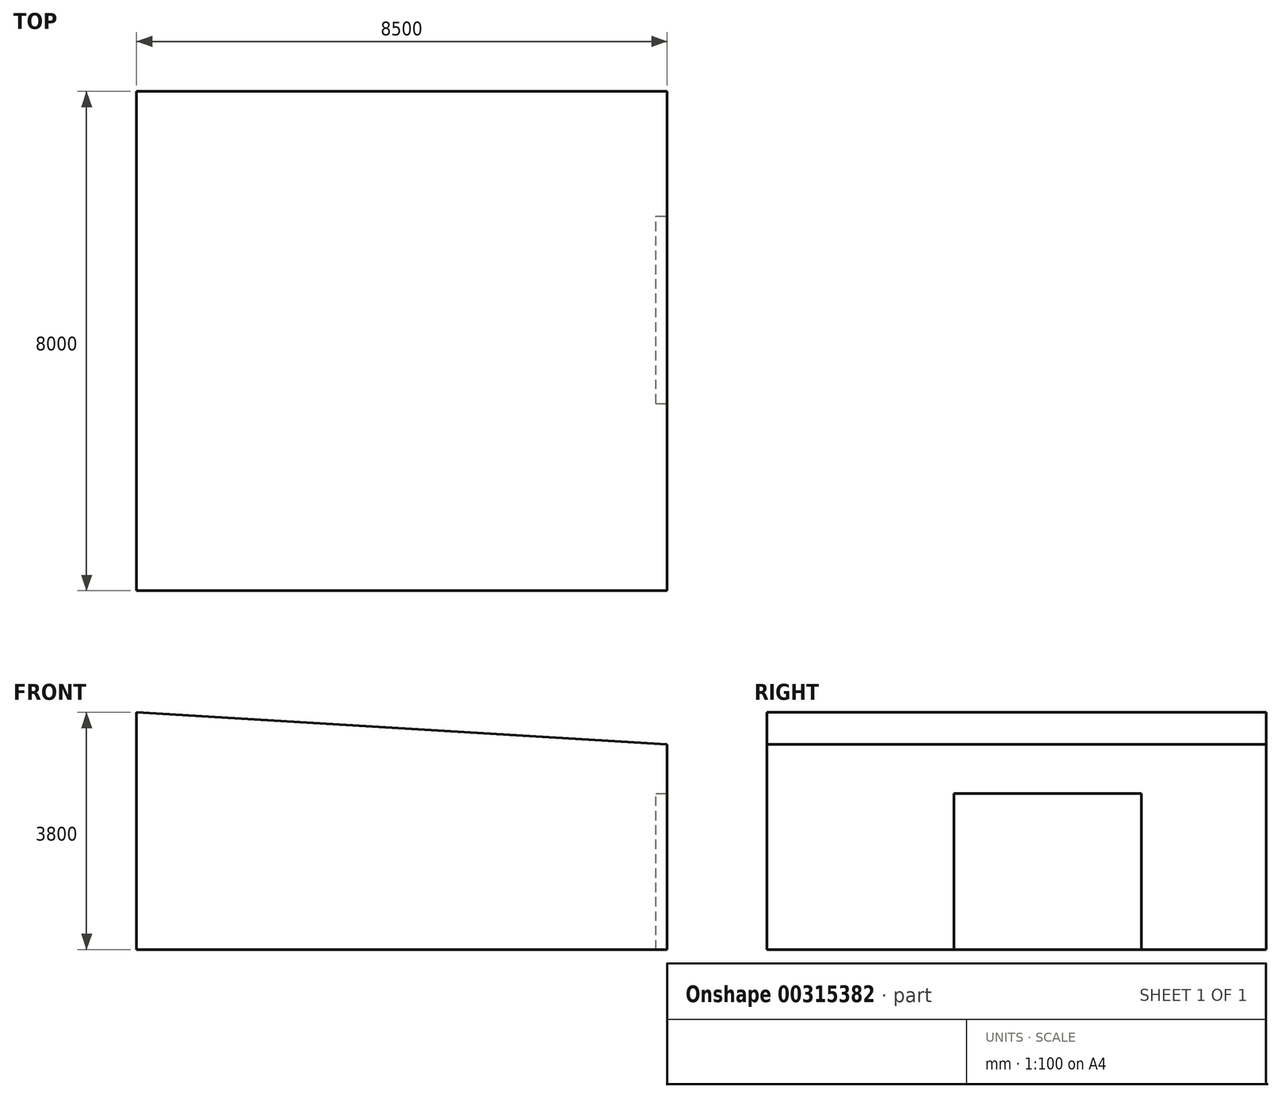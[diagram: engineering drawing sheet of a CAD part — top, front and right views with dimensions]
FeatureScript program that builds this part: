
annotation { "Feature Type Name" : "Feature", "Feature Type Description" : "" }
export const myFeature = defineFeature(function(context is Context, id is Id, definition is map)
    precondition{}
    {
        {
            var Q0;
            Q0=qCreatedBy(makeId("Front.planeOp"),FACE);
            var sketch = newSketch(context, id + "F0", { "sketchPlane" : qUnion([Q0])});
            skLineSegment(sketch, "E0.bottom", {"start": v(0, 0) * mm, "end": v(-5000, 0) * mm});
            skLineSegment(sketch, "E0.top", {"start": v(0, 3500) * mm, "end": v(-5000, 3500) * mm});
            skLineSegment(sketch, "E0.left", {"start": v(0, 0) * mm, "end": v(0, 3500) * mm});
            skLineSegment(sketch, "E0.right", {"start": v(-5000, 0) * mm, "end": v(-5000, 3500) * mm});
            skLineSegment(sketch, "E1", {"start": v(-5000, 3500) * mm, "end": v(-5000, 3800) * mm});
            skLineSegment(sketch, "E2", {"start": v(-5000, 3800) * mm, "end": v(0, 3500) * mm});
            skLineSegment(sketch, "E3", {"start": v(0, 0) * mm, "end": v(3500, 0) * mm});
            skLineSegment(sketch, "E4", {"start": v(3500, 0) * mm, "end": v(3500, 3290) * mm});
            skLineSegment(sketch, "E5", {"start": v(3500, 3290) * mm, "end": v(0, 3500) * mm});
            skSolve(sketch);
        }
        {
            var Q0;
            Q0 = qSketchRegion(id + "F0", true);
            extrude(context, id + "F1", {"entities" : qUnion([Q0]), "oppositeDirection" : true, "depth" : 8000 * mm});
        }
        {
            var Q0;
            Q0=makeQuery(id+"F1.opExtrude","SWEPT_FACE",FACE,{"disambiguationData":[OSD([sQuery(id+"F0.wireOp",EDGE,"E4")])]});
            cPlane(context, id + "F2", {"entities" : qUnion([Q0]), "cplaneType" : CPlaneType.OFFSET, "offset" : 25 * mm, "width" : 150 * mm, "height" : 150 * mm});
        }
        {
            var Q0;
            Q0=qCreatedBy(id+"F2.planeOp",FACE);
            var sketch = newSketch(context, id + "F3", { "sketchPlane" : qUnion([Q0])});
            skLineSegment(sketch, "E6.bottom", {"start": v(3000, 0) * mm, "end": v(6000, 0) * mm});
            skLineSegment(sketch, "E6.top", {"start": v(3000, 2500) * mm, "end": v(6000, 2500) * mm});
            skLineSegment(sketch, "E6.left", {"start": v(3000, 0) * mm, "end": v(3000, 2500) * mm});
            skLineSegment(sketch, "E6.right", {"start": v(6000, 0) * mm, "end": v(6000, 2500) * mm});
            skSolve(sketch);
        }
        {
            var Q0;
            Q0=makeQuery(id+"F3.imprint","IMPRINT",FACE,{"disambiguationData":[TD([[makeQuery(id+"F3.imprint","IMPRINT",EDGE,{"derivedFrom":sQuery(id+"F3.wireOp",EDGE,"E6.bottom")}),1.0]])]});
            extrude(context, id + "F4", {"entities" : qUnion([Q0]), "operationType" : NewBodyOperationType.REMOVE, "oppositeDirection" : true, "depth" : 200 * mm});
        }
    });
